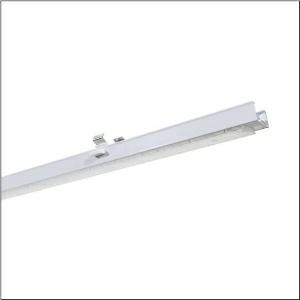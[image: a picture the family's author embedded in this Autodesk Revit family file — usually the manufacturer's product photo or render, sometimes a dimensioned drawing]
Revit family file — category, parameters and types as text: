
# Revit family: trunking_flex_31_51re12mb18b
name_source: partatom
category: Lighting Fixtures
units: mm (PartAtom-declared; Revit-internal decimal feet)

## family parameters
Cut with Voids When Loaded = No
Host = Face
Light Source = No
Part Type = Normal
Room Calculation Point = No
Round Connector Dimension = Use Diameter
Shared = No

## types (1)
- --- (1 x LED, 8000 lm, 50 W, 3500K)
    Apparent Load = 50 VA
    CIE Flux Codes = 65 91 98 99 100
    Color Rendering = 80
    Color Temperature = 3500K
    Default Elevation = 1800 mm
    Description = Trunking Flex 31, luminaire insert, of extruded aluminium section, coated, traffic white (RAL 9016), length: 1.472mm, width: 91mm, height: 53mm, LED rated luminous flux: 8.000lm, light colour: 835, control gear: ON/OFF Multilumen, with system connector: socket, mains connection: 220..240V, AC, 50/60Hz, rated input power: 50W, luminous flux adjustable on luminaire in four steps (4130/5610/6850/8000lm), connected load according to luminous flux setting (25/34/42/50W), primary light control with lens, of plastic, primary optical cover: cover, of PMMA, light emission: direct distribution, protection rating (complete): IP20, insulation class (complete): insulation class I (protective earthing), certification: CE, UKCA, impact resistance: IK02, permissible ambient temperature for indoor applications: -20..+40°C, packaging unit: 1 piece
    Height = 58 mm
    Lamp = 1 x LED
    Lamp Light Flux = 8000 lm
    Lamp Power = 50 W
    Lamp count = 1
    Length = 1472 mm
    Luminous efficacy = 160 lm/W
    Manufacturer = Siteco
    ModVariant = No
    Model = 51RE12MB18B
    Mounting Place = Ceiling
    Mounting Type = Pendant
    Number of Poles = 1
    OnlyDefault = Yes
    Power Factor = 1
    Product Name = Trunking Flex 31
    Product group = luminaire insert
    ProductGroupID = 902
    Protection Class = Protection class I
    Protection Degree = IP 20
    RLX_Detail_Level = 1
    RLX_Emergency_Light_Flux = 0 lm
    RLX_Emergency_Type = 0
    RLX_Emergency_Type_DB = No
    RlxData = <blob elided: 20317 chars, md5=d104f56e>
    Socket = socket
    Standby Power = 0 W
    System Light Flux = 8000 lm
    System Power = 50 W
    Type Comments = factory setting: luminous flux: 100 % | (ON | ON) | 300 mA
    Type Image = l_1266702.jpg
    URL = http://relux.com
    VarID = @adj_059174
    Voltage = 0 V
    Weight = 0.00 kg
    Width = 65 mm

## geometry (parser evidence)
native form markers: Blend x4, Sweep x13
no freeform markers — native parametric forms only
